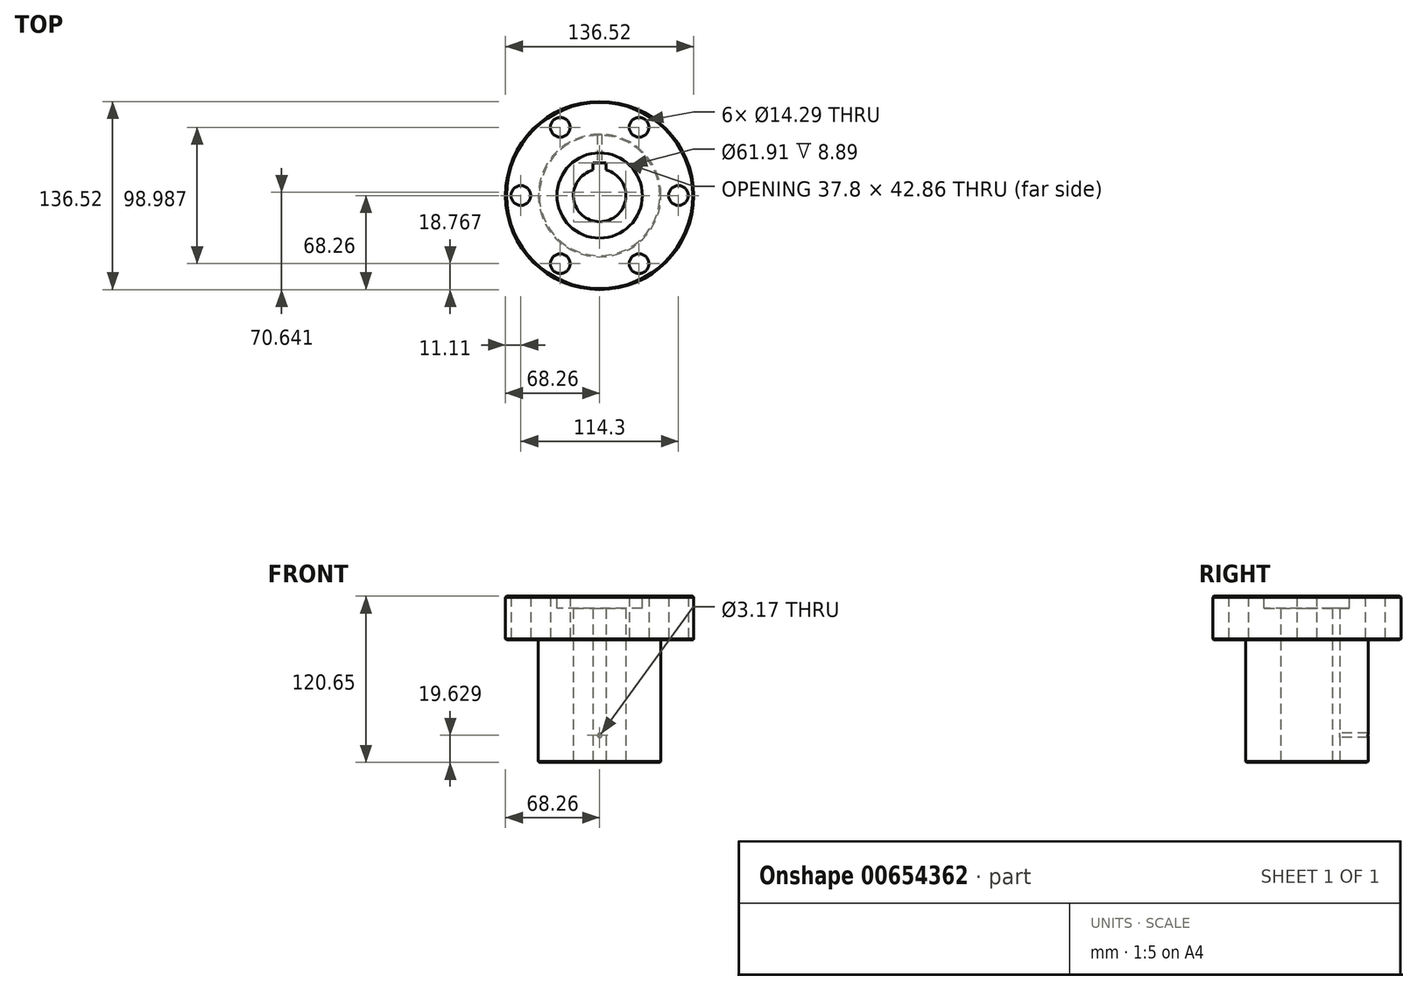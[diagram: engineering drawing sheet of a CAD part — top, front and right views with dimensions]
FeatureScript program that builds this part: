
annotation { "Feature Type Name" : "Feature", "Feature Type Description" : "" }
export const myFeature = defineFeature(function(context is Context, id is Id, definition is map)
    precondition{}
    {
        {
            var Q0;
            Q0=qCreatedBy(makeId("Top.planeOp"),FACE);
            var sketch = newSketch(context, id + "F0", { "sketchPlane" : qUnion([Q0])});
            skCircle(sketch, "E0", {"center": v(0, 0) * mm, "radius": 68.26 * mm});
            skCircle(sketch, "E1", {"center": v(0, 0) * mm, "radius": 19.05 * mm});
            skCircle(sketch, "E2", {"center": v(0, 0) * mm, "radius": 57.15 * mm, "construction": true});
            skLineSegment(sketch, "E3", {"start": v(0, 0) * mm, "end": v(0, 110.28) * mm, "construction": true});
            skLineSegment(sketch, "E4", {"start": v(0, 0) * mm, "end": v(56.56, 97.97) * mm, "construction": true});
            skCircle(sketch, "E5", {"center": v(28.58, 49.5) * mm, "radius": 7.14 * mm});
            skCircle(sketch, "E6.1.0", {"center": v(-28.57, 49.5) * mm, "radius": 7.14 * mm});
            skCircle(sketch, "E6.2.0", {"center": v(-57.15, 0) * mm, "radius": 7.14 * mm});
            skCircle(sketch, "E6.3.0", {"center": v(-28.58, -49.5) * mm, "radius": 7.14 * mm});
            skCircle(sketch, "E6.4.0", {"center": v(28.57, -49.5) * mm, "radius": 7.14 * mm});
            skCircle(sketch, "E6.5.0", {"center": v(57.15, 0) * mm, "radius": 7.14 * mm});
            skSolve(sketch);
        }
        {
            var Q0;
            Q0=qSketchRegion(id+"F0",true);
            extrude(context, id + "F1", {"entities" : qUnion([Q0]), "depth" : 31.75 * mm, "offsetDistance" : 25.4 * mm});
        }
        {
            var Q0;
            Q0=makeQuery(id+"F1.opExtrude","CAP_FACE",FACE,{"disambiguationData":[OSD([sQuery(id+"F0.wireOp",EDGE,"E0"),sQuery(id+"F0.wireOp",EDGE,"E1"),sQuery(id+"F0.wireOp",EDGE,"E5"),sQuery(id+"F0.wireOp",EDGE,"E6.1.0"),sQuery(id+"F0.wireOp",EDGE,"E6.2.0"),sQuery(id+"F0.wireOp",EDGE,"E6.3.0"),sQuery(id+"F0.wireOp",EDGE,"E6.4.0"),sQuery(id+"F0.wireOp",EDGE,"E6.5.0")])],"isStart":false});
            var sketch = newSketch(context, id + "F2", { "sketchPlane" : qUnion([Q0])});
            skCircle(sketch, "E7", {"center": v(0, 0) * mm, "radius": 30.96 * mm});
            skSolve(sketch);
        }
        {
            var Q0;
            Q0=qSketchRegion(id+"F2",true);
            extrude(context, id + "F3", {"entities" : qUnion([Q0]), "operationType" : NewBodyOperationType.REMOVE, "oppositeDirection" : true, "depth" : 8.9 * mm, "offsetDistance" : 25.4 * mm});
        }
        {
            var Q0;
            Q0=makeQuery(id+"F1.opExtrude","CAP_FACE",FACE,{"disambiguationData":[OSD([sQuery(id+"F0.wireOp",EDGE,"E0"),sQuery(id+"F0.wireOp",EDGE,"E1"),sQuery(id+"F0.wireOp",EDGE,"E5"),sQuery(id+"F0.wireOp",EDGE,"E6.1.0"),sQuery(id+"F0.wireOp",EDGE,"E6.2.0"),sQuery(id+"F0.wireOp",EDGE,"E6.3.0"),sQuery(id+"F0.wireOp",EDGE,"E6.4.0"),sQuery(id+"F0.wireOp",EDGE,"E6.5.0")])],"isStart":true});
            var sketch = newSketch(context, id + "F4", { "sketchPlane" : qUnion([Q0])});
            skCircle(sketch, "E8", {"center": v(0, 0) * mm, "radius": 44.45 * mm});
            skCircle(sketch, "E9", {"center": v(0, 0) * mm, "radius": 19.05 * mm});
            skSolve(sketch);
        }
        {
            var Q0;
            Q0=qSketchRegion(id+"F4",true);
            extrude(context, id + "F5", {"entities" : qUnion([Q0]), "operationType" : NewBodyOperationType.ADD, "depth" : 88.9 * mm, "offsetDistance" : 25.4 * mm});
        }
        {
            var Q0;
            Q0=makeQuery(id+"F5.opExtrude","CAP_FACE",FACE,{"disambiguationData":[OSD([sQuery(id+"F4.wireOp",EDGE,"E8"),sQuery(id+"F4.wireOp",EDGE,"E9")])],"isStart":false});
            var sketch = newSketch(context, id + "F6", { "sketchPlane" : qUnion([Q0])});
            skLineSegment(sketch, "E10", {"start": v(0, 0) * mm, "end": v(0, -19.05) * mm});
            skLineSegment(sketch, "E11", {"start": v(0, -19.05) * mm, "end": v(0, -23.81) * mm});
            skLineSegment(sketch, "E12", {"start": v(0, -23.81) * mm, "end": v(-4.76, -23.81) * mm});
            skLineSegment(sketch, "E13", {"start": v(-4.76, -23.81) * mm, "end": v(-4.76, -10.52) * mm});
            skLineSegment(sketch, "E14", {"start": v(-4.76, -10.52) * mm, "end": v(4.76, -10.52) * mm});
            skLineSegment(sketch, "E15", {"start": v(4.76, -10.52) * mm, "end": v(4.76, -23.81) * mm});
            skLineSegment(sketch, "E16", {"start": v(4.76, -23.81) * mm, "end": v(0, -23.81) * mm});
            skSolve(sketch);
        }
        {
            var Q0;
            Q0=qSketchRegion(id+"F6",true);
            extrude(context, id + "F7", {"entities" : qUnion([Q0]), "operationType" : NewBodyOperationType.REMOVE, "endBound" : BoundingType.THROUGH_ALL, "oppositeDirection" : true, "depth" : 25.4 * mm, "offsetDistance" : 25.4 * mm});
        }
        {
            var Q0;
            Q0=makeQuery(id+"F1.opExtrude","CAP_EDGE",EDGE,{"disambiguationData":[OSD([sQuery(id+"F0.wireOp",EDGE,"E0")])],"isStart":false});
            var Q1;
            Q1=makeQuery(id+"F1.opExtrude","CAP_EDGE",EDGE,{"disambiguationData":[OSD([sQuery(id+"F0.wireOp",EDGE,"E0")])],"isStart":true});
            var Q2;
            Q2=makeQuery(id+"F3.boolean.opBoolean","COPY",EDGE,{"derivedFrom":makeQuery(id+"F3.opExtrude","CAP_EDGE",EDGE,{"disambiguationData":[OSD([sQuery(id+"F2.wireOp",EDGE,"E7")])],"isStart":true})});
            var Q3;
            Q3=makeQuery(id+"F5.opExtrude","CAP_EDGE",EDGE,{"disambiguationData":[OSD([sQuery(id+"F4.wireOp",EDGE,"E8")])],"isStart":false});
            chamfer(context, id + "F8", {"entities" : qUnion([Q0, Q1, Q2, Q3]), "width" : 0.76 * mm, "tangentPropagation" : true});
        }
        {
            var Q0;
            Q0=qCreatedBy(makeId("Front.planeOp"),FACE);
            var sketch = newSketch(context, id + "F9", { "sketchPlane" : qUnion([Q0])});
            skCircle(sketch, "E17", {"center": v(0, -69.27) * mm, "radius": 1.59 * mm});
            skSolve(sketch);
        }
        {
            var Q0;
            Q0=qSketchRegion(id+"F9",true);
            extrude(context, id + "F10", {"entities" : qUnion([Q0]), "operationType" : NewBodyOperationType.REMOVE, "oppositeDirection" : true, "depth" : 76.2 * mm, "offsetDistance" : 25.4 * mm});
        }
    });
